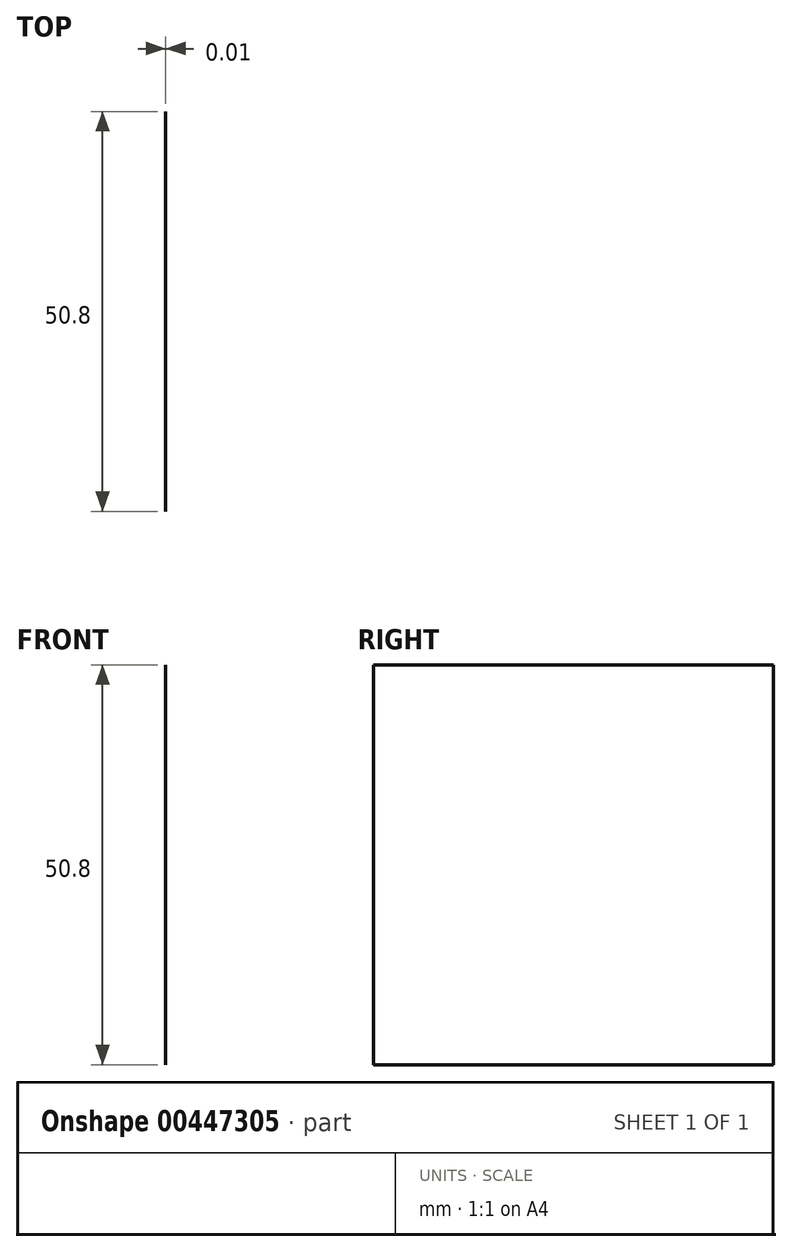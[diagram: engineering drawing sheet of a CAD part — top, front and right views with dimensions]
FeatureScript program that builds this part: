
annotation { "Feature Type Name" : "Feature", "Feature Type Description" : "" }
export const myFeature = defineFeature(function(context is Context, id is Id, definition is map)
    precondition{}
    {
        {
            var Q0;
            Q0=qCreatedBy(makeId("Right.planeOp"),FACE);
            var sketch = newSketch(context, id + "F0", { "sketchPlane" : qUnion([Q0])});
            skLineSegment(sketch, "E0.bottom", {"start": v(-25.4, 25.4) * mm, "end": v(25.4, 25.4) * mm});
            skLineSegment(sketch, "E0.top", {"start": v(-25.4, -25.4) * mm, "end": v(25.4, -25.4) * mm});
            skLineSegment(sketch, "E0.left", {"start": v(-25.4, 25.4) * mm, "end": v(-25.4, -25.4) * mm});
            skLineSegment(sketch, "E0.right", {"start": v(25.4, 25.4) * mm, "end": v(25.4, -25.4) * mm});
            skPoint(sketch, "E0.middle", {"position": v(0, 0) * mm});
            skSolve(sketch);
        }
        {
            var Q0;
            Q0=makeQuery(id+"F0.imprint","IMPRINT",FACE,{"disambiguationData":[TD([[makeQuery(id+"F0.imprint","IMPRINT",EDGE,{"derivedFrom":sQuery(id+"F0.wireOp",EDGE,"E0.bottom")}),-1.0]])]});
            extrude(context, id + "F1", {"entities" : qUnion([Q0]), "depth" : 3 / 203.2 * mm});
        }
    });
